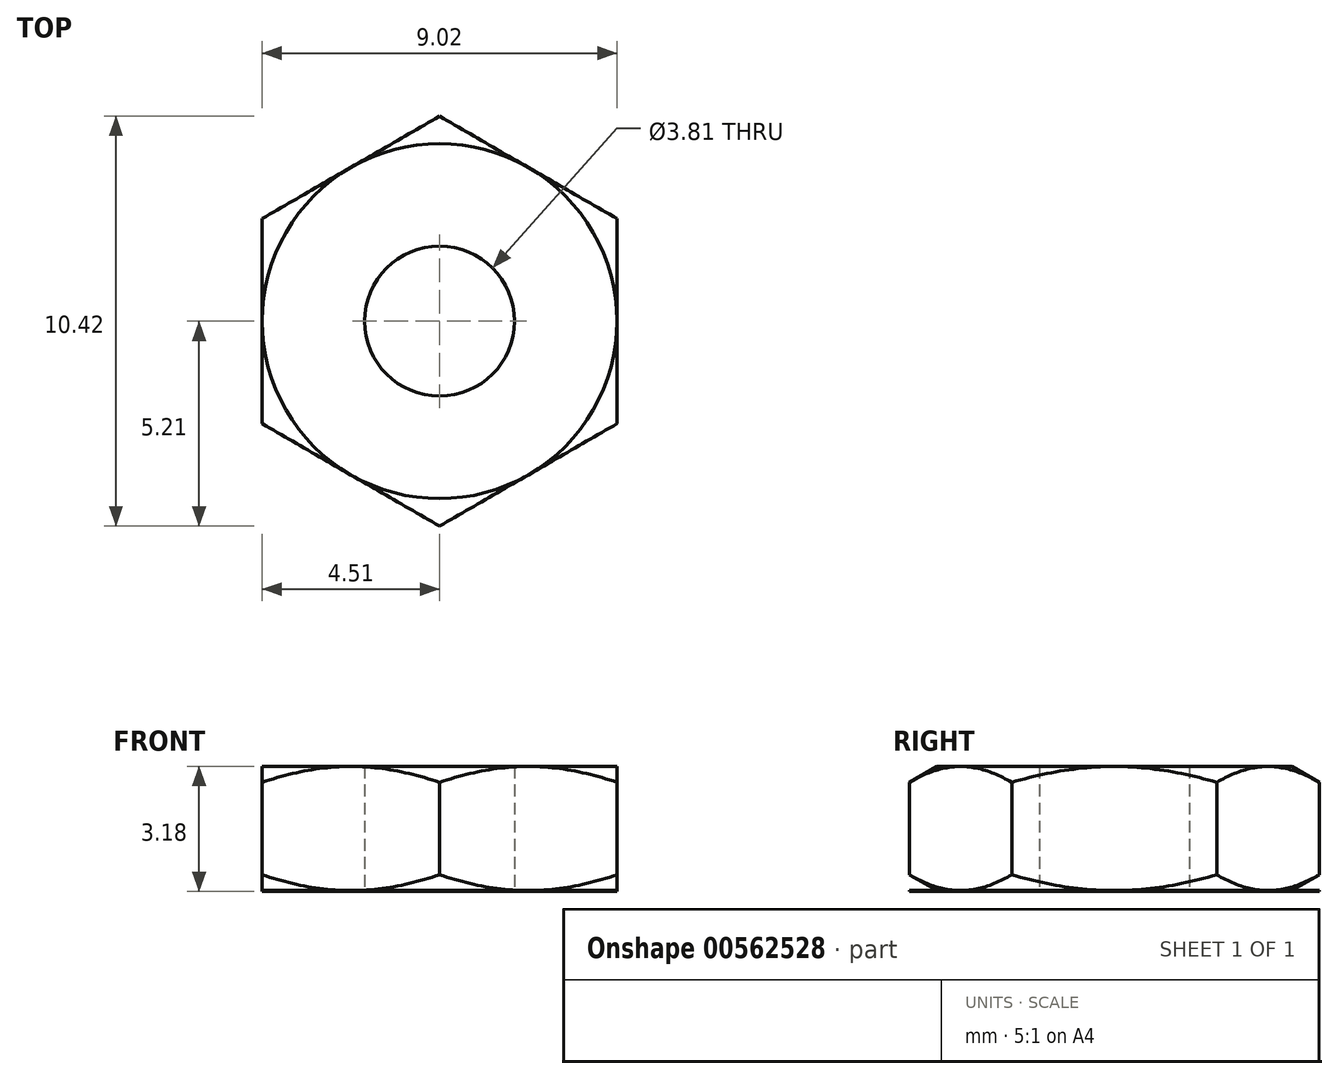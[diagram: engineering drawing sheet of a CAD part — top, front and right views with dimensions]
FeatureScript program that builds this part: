
annotation { "Feature Type Name" : "Feature", "Feature Type Description" : "" }
export const myFeature = defineFeature(function(context is Context, id is Id, definition is map)
    precondition{}
    {
        {
            var Q0;
            Q0=qCreatedBy(makeId("Top.planeOp"),FACE);
            var sketch = newSketch(context, id + "F0", { "sketchPlane" : qUnion([Q0])});
            skCircle(sketch, "E0.cCircle", {"center": v(0, 0) * mm, "radius": 4.5 * mm, "construction": true});
            skLineSegment(sketch, "E0.0", {"start": v(4.5, 2.6) * mm, "end": v(4.5, -2.6) * mm});
            skLineSegment(sketch, "E0.1", {"start": v(4.5, -2.6) * mm, "end": v(0, -5.2) * mm});
            skLineSegment(sketch, "E0.2", {"start": v(0, -5.2) * mm, "end": v(-4.5, -2.6) * mm});
            skLineSegment(sketch, "E0.3", {"start": v(-4.5, -2.6) * mm, "end": v(-4.5, 2.6) * mm});
            skLineSegment(sketch, "E0.4", {"start": v(-4.5, 2.6) * mm, "end": v(0, 5.2) * mm});
            skLineSegment(sketch, "E0.5", {"start": v(0, 5.2) * mm, "end": v(4.5, 2.6) * mm});
            skPoint(sketch, "E0.0.midPoint", {"position": v(4.5, 0) * mm});
            skCircle(sketch, "E1", {"center": v(0, 0) * mm, "radius": 1.9 * mm});
            skSolve(sketch);
        }
        {
            var Q0;
            Q0 = qSketchRegion(id + "F0", true);
            extrude(context, id + "F1", {"entities" : qUnion([Q0]), "depth" : 3.17 * mm, "offsetDistance" : 25.4 * mm});
        }
        {
            var Q0;
            Q0=qCreatedBy(makeId("Front.planeOp"),FACE);
            var sketch = newSketch(context, id + "F2", { "sketchPlane" : qUnion([Q0])});
            skLineSegment(sketch, "E2", {"start": v(0, 3.2) * mm, "end": v(0, 0) * mm, "construction": true});
            skLineSegment(sketch, "E3", {"start": v(0, 1.6) * mm, "end": v(4.54, 1.6) * mm, "construction": true});
            skLineSegment(sketch, "E4", {"start": v(4.5, 3.18) * mm, "end": v(5.96, 3.18) * mm});
            skLineSegment(sketch, "E5", {"start": v(5.96, 3.18) * mm, "end": v(5.96, 2.34) * mm});
            skLineSegment(sketch, "E6", {"start": v(5.96, 2.34) * mm, "end": v(4.5, 3.18) * mm});
            skLineSegment(sketch, "E7.MirrorCS", {"start": v(4.5, 0.02) * mm, "end": v(5.96, 0.02) * mm});
            skLineSegment(sketch, "E8.MirrorCS", {"start": v(5.96, 0.02) * mm, "end": v(5.96, 0.86) * mm});
            skLineSegment(sketch, "E9.MirrorCS", {"start": v(5.96, 0.86) * mm, "end": v(4.5, 0.02) * mm});
            skSolve(sketch);
        }
        {
            var Q0;
            Q0 = qSketchRegion(id + "F2", true);
            var Q1;
            Q1=sQuery(id+"F2.wireOp",EDGE,"E2");
            revolve(context, id + "F3", {"operationType" : NewBodyOperationType.REMOVE, "entities" : qUnion([Q0]), "axis" : qUnion([Q1]), "revolveType" : RevolveType.FULL, "oppositeDirection" : true});
        }
    });
